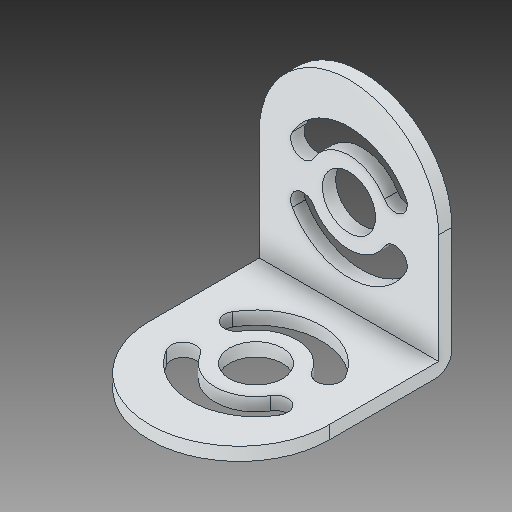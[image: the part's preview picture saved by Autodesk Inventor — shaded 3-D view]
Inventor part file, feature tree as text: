
AUTODESK INVENTOR PART (.ipt)
format: ipt  version: 2018 (Build 220112000, 112)  size: 183,808 bytes
history: native  units: in
note: dims shown in document units (in); Inventor stores cm internally (conversion verified against a paired STEP export)
features: fillet x1
ambient origin geometry x8: Origin, YZ Plane, XZ Plane, XY Plane, X Axis, Y Axis, Z Axis, Center Point
bodies: Solid1 (feature_tree)
feature tree (1):
  fillet  "Fillet2"  [1 undecoded]
note: 1 required parameter value undecoded (feature->parameter linkage not recoverable at this tier; creation-order binding heuristic only, values carry confidence <= 0.55)
